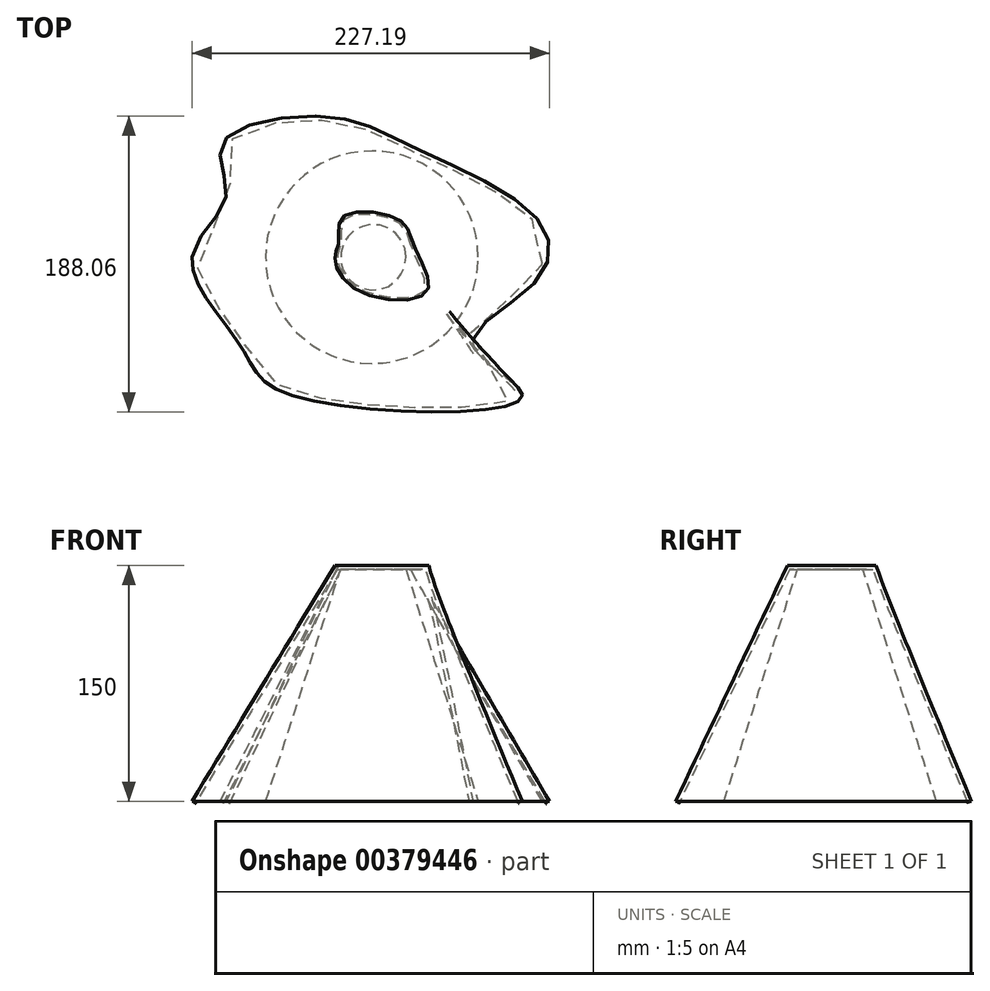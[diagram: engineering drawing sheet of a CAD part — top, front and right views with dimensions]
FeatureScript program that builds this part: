
annotation { "Feature Type Name" : "Feature", "Feature Type Description" : "" }
export const myFeature = defineFeature(function(context is Context, id is Id, definition is map)
    precondition{}
    {
        {
            var Q0;
            Q0=qCreatedBy(makeId("Top.planeOp"),FACE);
            var sketch = newSketch(context, id + "F0", { "sketchPlane" : qUnion([Q0])});
            skPoint(sketch, "E0.0.internal.orphan", {"position": v(-38.49, 0) * mm});
            skPoint(sketch, "E1.5.internal.orphan", {"position": v(-121.8, 0) * mm});
            skFitSpline(sketch, "E2", {"points": [v(-121.8, 0) * mm, v(-100.4, 37.92) * mm, v(-102.78, 72.01) * mm, v(-36.58, 89.45) * mm, v(20.11, 69.24) * mm, v(98.6, 22.85) * mm, v(96.23, -16) * mm, v(56.98, -56.04) * mm, v(87.9, -88.54) * mm, v(-58.78, -87.75) * mm, v(-91.28, -56.04) * mm, v(-121.8, 0) * mm]});
            skSolve(sketch);
        }
        {
            var Q0;
            Q0=qCreatedBy(makeId("Top.planeOp"),FACE);
            cPlane(context, id + "F1", {"entities" : qUnion([Q0]), "cplaneType" : CPlaneType.OFFSET, "offset" : 150 * mm, "width" : 150 * mm, "height" : 150 * mm});
        }
        {
            var Q0;
            Q0=qCreatedBy(id+"F1.planeOp",FACE);
            var sketch = newSketch(context, id + "F2", { "sketchPlane" : qUnion([Q0])});
            skFitSpline(sketch, "E3", {"points": [v(-17.26, -20.71) * mm, v(-31.07, 0) * mm, v(-28.77, 9.2) * mm, v(-25.6, 25.9) * mm, v(10.07, 23.6) * mm, v(18.99, 7.48) * mm, v(27.33, -21.87) * mm, v(-17.26, -20.71) * mm]});
            skPoint(sketch, "E4.center.orphan", {"position": v(-7.06, 0) * mm});
            skSolve(sketch);
        }
        {
            var Q0;
            Q0=makeQuery(id+"F0.imprint","IMPRINT",FACE,{"disambiguationData":[TD([[makeQuery(id+"F0.imprint","IMPRINT",EDGE,{"derivedFrom":sQuery(id+"F0.wireOp",EDGE,"E2")}),-1.0]])]});
            var Q1;
            Q1=makeQuery(id+"F2.imprint","IMPRINT",FACE,{"disambiguationData":[TD([[makeQuery(id+"F2.imprint","IMPRINT",EDGE,{"derivedFrom":sQuery(id+"F2.wireOp",EDGE,"E3")}),-1.0]])]});
            loft(context, id + "F3", {"sheetProfilesArray" : [{ "sheetProfileEntities" : qUnion([Q0]) }, { "sheetProfileEntities" : qUnion([Q1]) }]});
        }
        {
            var Q0;
            Q0=qCreatedBy(id+"F1.planeOp",FACE);
            var sketch = newSketch(context, id + "F4", { "sketchPlane" : qUnion([Q0])});
            skCircle(sketch, "E5", {"center": v(-6.68, 0) * mm, "radius": 20 * mm});
            skSolve(sketch);
        }
        {
            var Q0;
            Q0=makeQuery(id+"F0.imprint","IMPRINT",FACE,{"disambiguationData":[TD([[makeQuery(id+"F0.imprint","IMPRINT",EDGE,{"derivedFrom":sQuery(id+"F0.wireOp",EDGE,"E2")}),-1.0]])]});
            var sketch = newSketch(context, id + "F5", { "sketchPlane" : qUnion([Q0])});
            skCircle(sketch, "E6", {"center": v(-7.55, 0) * mm, "radius": 67.5 * mm});
            skSolve(sketch);
        }
        {
            var Q1;
            Q1=makeQuery(id+"F5.imprint","IMPRINT",FACE,{"disambiguationData":[TD([[makeQuery(id+"F5.imprint","IMPRINT",EDGE,{"derivedFrom":sQuery(id+"F5.wireOp",EDGE,"E6")}),1.0]])]});
            var Q2;
            Q2=makeQuery(id+"F4.imprint","IMPRINT",FACE,{"disambiguationData":[TD([[makeQuery(id+"F4.imprint","IMPRINT",EDGE,{"derivedFrom":sQuery(id+"F4.wireOp",EDGE,"E5")}),1.0]])]});
            loft(context, id + "F6", {"operationType" : NewBodyOperationType.ADD, "sheetProfilesArray" : [{ "sheetProfileEntities" : qUnion([Q1]) }, { "sheetProfileEntities" : qUnion([Q2]) }]});
        }
        {
            var Q0;
            Q0=makeQuery(id+"F3.opLoft","CAP_FACE",FACE,{"disambiguationData":[OSD([makeQuery(id+"F0.imprint","IMPRINT",FACE,{"disambiguationData":[TD([[makeQuery(id+"F0.imprint","IMPRINT",EDGE,{"derivedFrom":sQuery(id+"F0.wireOp",EDGE,"E2")}),-1.0]])]})])],"isStart":true});
            shell(context, id + "F7", {"entities" : qUnion([Q0]), "thickness" : 2.5 * mm});
        }
        {
            var Q1;
            Q1=makeQuery(id+"F4.imprint","IMPRINT",FACE,{"disambiguationData":[TD([[makeQuery(id+"F4.imprint","IMPRINT",EDGE,{"derivedFrom":sQuery(id+"F4.wireOp",EDGE,"E5")}),1.0]])]});
            var Q2;
            Q2=makeQuery(id+"F5.imprint","IMPRINT",FACE,{"disambiguationData":[TD([[makeQuery(id+"F5.imprint","IMPRINT",EDGE,{"derivedFrom":sQuery(id+"F5.wireOp",EDGE,"E6")}),1.0]])]});
            loft(context, id + "F8", {"operationType" : NewBodyOperationType.ADD, "sheetProfilesArray" : [{ "sheetProfileEntities" : qUnion([Q1]) }, { "sheetProfileEntities" : qUnion([Q2]) }]});
        }
    });
